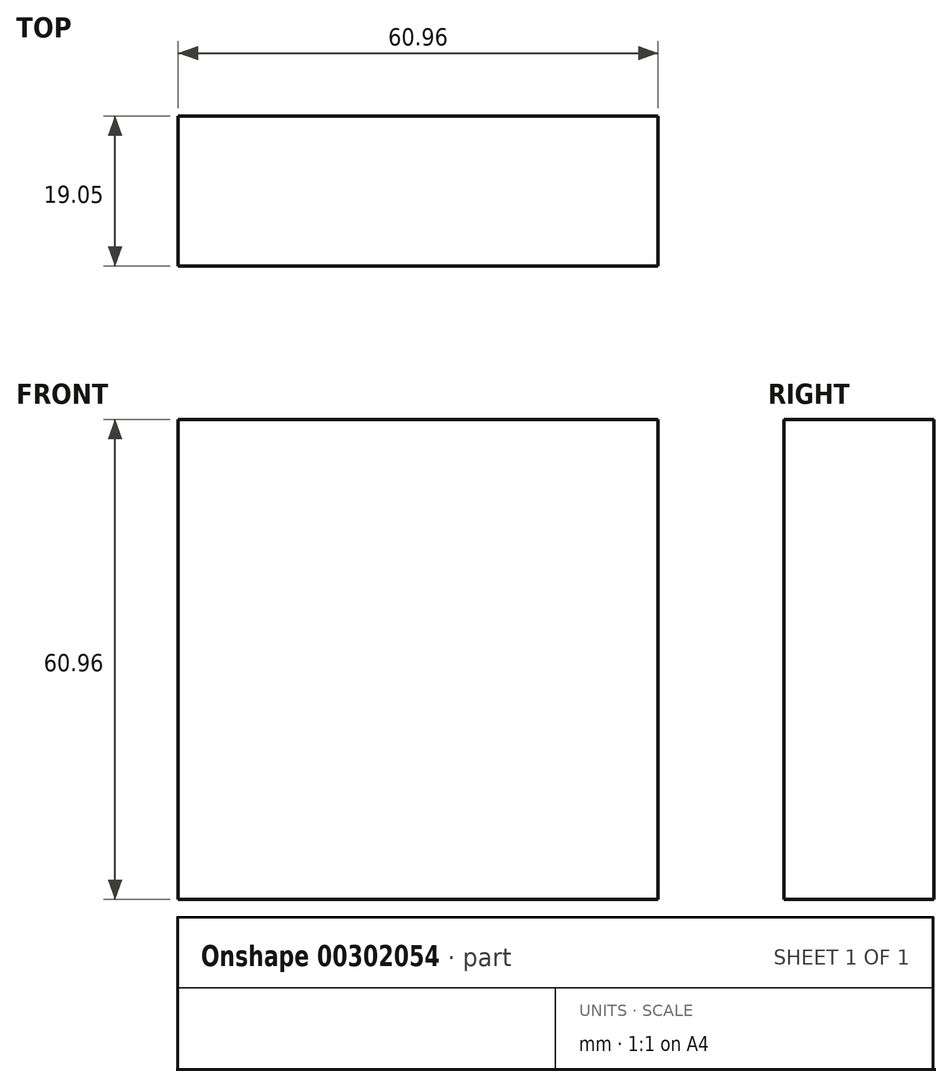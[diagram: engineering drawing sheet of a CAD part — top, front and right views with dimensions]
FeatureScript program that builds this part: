
annotation { "Feature Type Name" : "Feature", "Feature Type Description" : "" }
export const myFeature = defineFeature(function(context is Context, id is Id, definition is map)
    precondition{}
    {
        {
            var Q0;
            Q0=qCreatedBy(makeId("Front.planeOp"),FACE);
            cPlane(context, id + "F0", {"entities" : qUnion([Q0]), "cplaneType" : CPlaneType.OFFSET, "offset" : 25.4 * mm, "width" : 152.4 * mm, "height" : 152.4 * mm});
        }
        {
            var Q0;
            Q0=qCreatedBy(id+"F0.planeOp",FACE);
            var sketch = newSketch(context, id + "F1", { "sketchPlane" : qUnion([Q0])});
            skLineSegment(sketch, "E0.bottom", {"start": v(0, 0) * mm, "end": v(60.96, 0) * mm});
            skLineSegment(sketch, "E0.top", {"start": v(0, 60.96) * mm, "end": v(60.96, 60.96) * mm});
            skLineSegment(sketch, "E0.left", {"start": v(0, 0) * mm, "end": v(0, 60.96) * mm});
            skLineSegment(sketch, "E0.right", {"start": v(60.96, 0) * mm, "end": v(60.96, 60.96) * mm});
            skSolve(sketch);
        }
        {
            var Q0;
            Q0=makeQuery(id+"F1.imprint","IMPRINT",FACE,{"disambiguationData":[TD([[makeQuery(id+"F1.imprint","IMPRINT",EDGE,{"derivedFrom":sQuery(id+"F1.wireOp",EDGE,"E0.bottom")}),1.0]])]});
            extrude(context, id + "F2", {"entities" : qUnion([Q0]), "depth" : 19.05 * mm});
        }
    });
